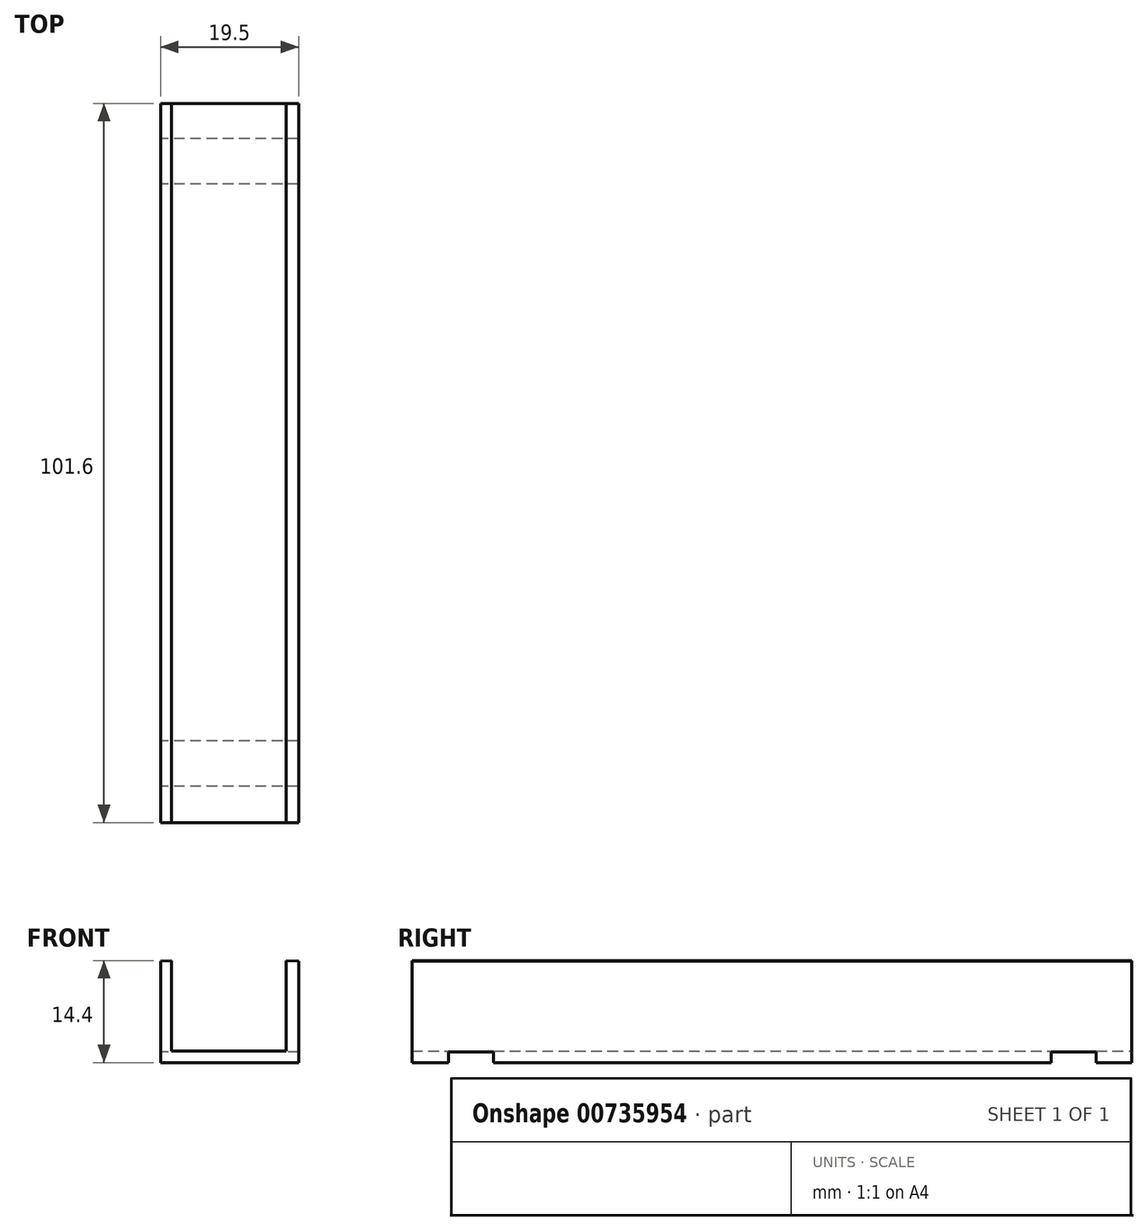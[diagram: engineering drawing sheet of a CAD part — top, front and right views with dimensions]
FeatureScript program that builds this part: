
annotation { "Feature Type Name" : "Feature", "Feature Type Description" : "" }
export const myFeature = defineFeature(function(context is Context, id is Id, definition is map)
    precondition{}
    {
        {
            var Q0;
            Q0=qCreatedBy(makeId("Front.planeOp"),FACE);
            var sketch = newSketch(context, id + "F0", { "sketchPlane" : qUnion([Q0])});
            skLineSegment(sketch, "E0.bottom", {"start": v(0, 0) * mm, "end": v(19.5, 0) * mm});
            skLineSegment(sketch, "E0.left", {"start": v(0, 0) * mm, "end": v(0, 14.34) * mm});
            skLineSegment(sketch, "E0.right", {"start": v(19.5, 0) * mm, "end": v(19.5, 14.34) * mm});
            skLineSegment(sketch, "E1.bottom", {"start": v(1.55, 1.62) * mm, "end": v(17.73, 1.62) * mm});
            skLineSegment(sketch, "E1.left", {"start": v(1.55, 1.62) * mm, "end": v(1.55, 14.4) * mm});
            skLineSegment(sketch, "E1.right", {"start": v(17.73, 1.62) * mm, "end": v(17.73, 14.4) * mm});
            skLineSegment(sketch, "E2", {"start": v(0, 14.34) * mm, "end": v(1.55, 14.4) * mm});
            skLineSegment(sketch, "E3", {"start": v(17.73, 14.4) * mm, "end": v(19.5, 14.34) * mm});
            skSolve(sketch);
        }
        {
            var Q0;
            Q0=makeQuery(id+"F0.imprint","IMPRINT",FACE,{"disambiguationData":[TD([[makeQuery(id+"F0.imprint","IMPRINT",EDGE,{"derivedFrom":sQuery(id+"F0.wireOp",EDGE,"E0.bottom")}),1.0]])]});
            extrude(context, id + "F1", {"entities" : qUnion([Q0]), "depth" : 101.6 * mm, "offsetDistance" : 25.4 * mm});
        }
        {
            var Q0;
            Q0=makeQuery(id+"F1.opExtrude","SWEPT_FACE",FACE,{"disambiguationData":[OSD([sQuery(id+"F0.wireOp",EDGE,"E0.left")])]});
            var sketch = newSketch(context, id + "F2", { "sketchPlane" : qUnion([Q0])});
            skLineSegment(sketch, "E4.bottom", {"start": v(5, 0) * mm, "end": v(11.38, 0) * mm});
            skLineSegment(sketch, "E4.top", {"start": v(5, 1.5) * mm, "end": v(11.38, 1.5) * mm});
            skLineSegment(sketch, "E4.left", {"start": v(5, 0) * mm, "end": v(5, 1.5) * mm});
            skLineSegment(sketch, "E4.right", {"start": v(11.38, 0) * mm, "end": v(11.38, 1.5) * mm});
            skLineSegment(sketch, "E5.MirrorCS", {"start": v(90.07, 0) * mm, "end": v(90.07, 1.5) * mm});
            skLineSegment(sketch, "E6.MirrorCS", {"start": v(96.44, 0) * mm, "end": v(96.44, 1.5) * mm});
            skLineSegment(sketch, "E7.MirrorCS", {"start": v(96.44, 0) * mm, "end": v(90.07, 0) * mm});
            skLineSegment(sketch, "E8.MirrorCS", {"start": v(96.44, 1.5) * mm, "end": v(90.07, 1.5) * mm});
            skSolve(sketch);
        }
        {
            var Q0;
            Q0=qSketchRegion(id+"F2",true);
            extrude(context, id + "F3", {"entities" : qUnion([Q0]), "operationType" : NewBodyOperationType.REMOVE, "endBound" : BoundingType.UP_TO_NEXT, "oppositeDirection" : true, "depth" : -25.4 * mm, "offsetDistance" : -12.7 * mm});
        }
    });
